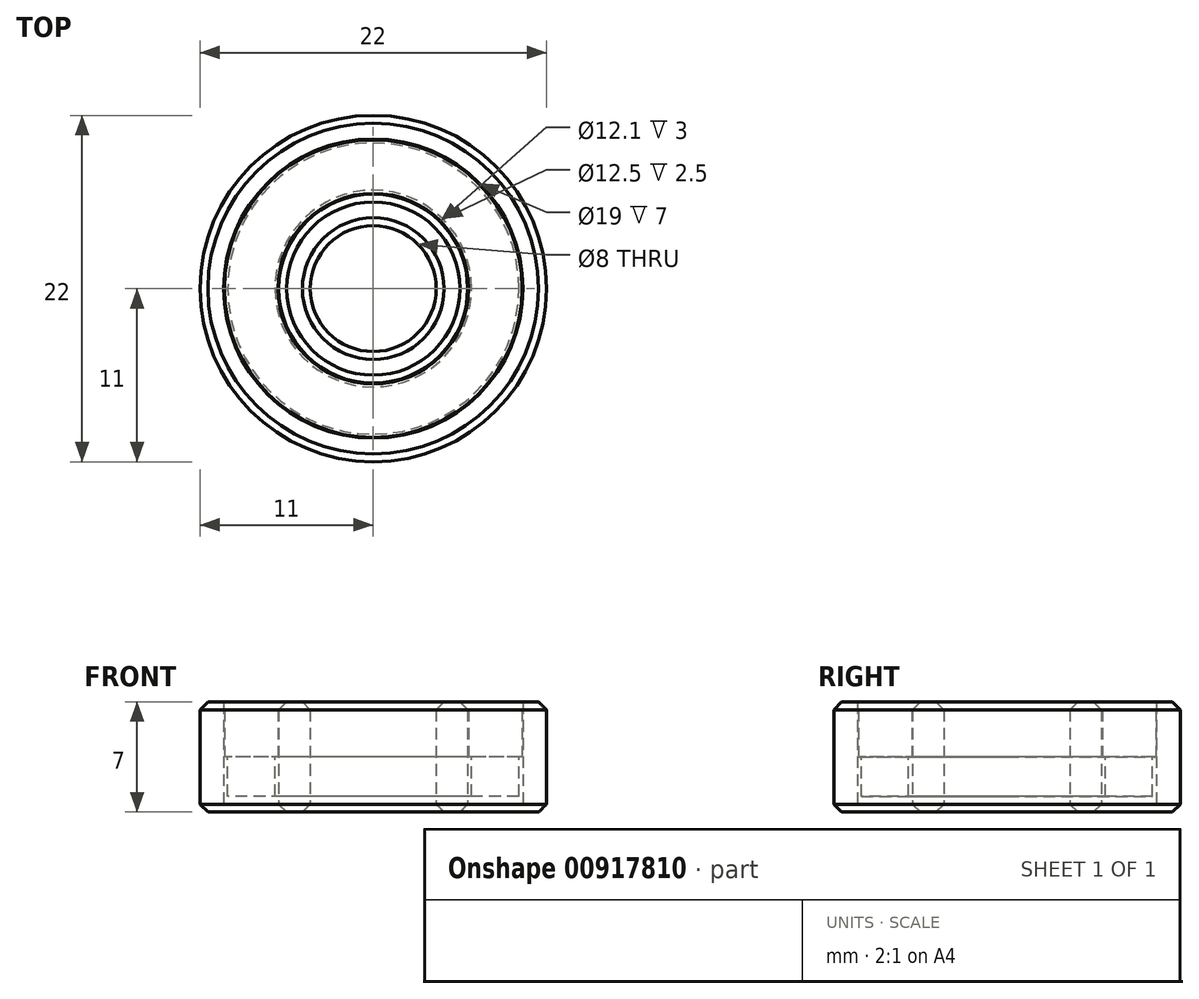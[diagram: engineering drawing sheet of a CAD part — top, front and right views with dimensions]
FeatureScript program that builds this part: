
annotation { "Feature Type Name" : "Feature", "Feature Type Description" : "" }
export const myFeature = defineFeature(function(context is Context, id is Id, definition is map)
    precondition{}
    {
        {
            var Q0;
            Q0=qCreatedBy(makeId("Top.planeOp"),FACE);
            var sketch = newSketch(context, id + "F0", { "sketchPlane" : qUnion([Q0])});
            skCircle(sketch, "E0", {"center": v(0, 0) * mm, "radius": 4 * mm});
            skCircle(sketch, "E1", {"center": v(0, 0) * mm, "radius": 6 * mm});
            skCircle(sketch, "E2", {"center": v(0, 0) * mm, "radius": 11 * mm});
            skCircle(sketch, "E3", {"center": v(0, 0) * mm, "radius": 9.5 * mm});
            skSolve(sketch);
        }
        {
            var Q0;
            Q0=makeQuery(id+"F0.imprint","IMPRINT",FACE,{"disambiguationData":[TD([[makeQuery(id+"F0.imprint","IMPRINT",EDGE,{"derivedFrom":sQuery(id+"F0.wireOp",EDGE,"E2")}),1.0]])]});
            var Q1;
            Q1=makeQuery(id+"F0.imprint","IMPRINT",FACE,{"disambiguationData":[TD([[makeQuery(id+"F0.imprint","IMPRINT",EDGE,{"derivedFrom":sQuery(id+"F0.wireOp",EDGE,"E0")}),-1.0]])]});
            extrude(context, id + "F1", {"entities" : qUnion([Q0, Q1]), "endBound" : BoundingType.SYMMETRIC, "depth" : 7 * mm, "offsetDistance" : 25 * mm});
        }
        {
            var Q0;
            Q0=qCreatedBy(makeId("Top.planeOp"),FACE);
            var sketch = newSketch(context, id + "F2", { "sketchPlane" : qUnion([Q0])});
            skCircle(sketch, "E4", {"center": v(0, 0) * mm, "radius": 6.25 * mm});
            skCircle(sketch, "E5", {"center": v(0, 0) * mm, "radius": 9.25 * mm});
            skSolve(sketch);
        }
        {
            var Q0;
            Q0=makeQuery(id+"F2.imprint","IMPRINT",FACE,{"disambiguationData":[TD([[makeQuery(id+"F2.imprint","IMPRINT",EDGE,{"derivedFrom":sQuery(id+"F2.wireOp",EDGE,"E4")}),-1.0]])]});
            extrude(context, id + "F3", {"entities" : qUnion([Q0]), "oppositeDirection" : true, "depth" : 2.5 * mm, "offsetDistance" : 25 * mm});
        }
        {
            var Q0;
            Q0=qCreatedBy(makeId("Top.planeOp"),FACE);
            var sketch = newSketch(context, id + "F4", { "sketchPlane" : qUnion([Q0])});
            skCircle(sketch, "E6", {"center": v(0, 0) * mm, "radius": 6.05 * mm});
            skCircle(sketch, "E7", {"center": v(0, 0) * mm, "radius": 9.45 * mm});
            skSolve(sketch);
        }
        {
            var Q0;
            Q0 = qSketchRegion(id + "F4", true);
            extrude(context, id + "F5", {"entities" : qUnion([Q0]), "depth" : 3 * mm, "offsetDistance" : 25 * mm});
        }
        {
            var Q0;
            Q0=makeQuery(id+"F1.opExtrude","CAP_EDGE",EDGE,{"disambiguationData":[OSD([sQuery(id+"F0.wireOp",EDGE,"E2")])],"isStart":false});
            var Q1;
            Q1=makeQuery(id+"F1.opExtrude","CAP_EDGE",EDGE,{"disambiguationData":[OSD([sQuery(id+"F0.wireOp",EDGE,"E2")])],"isStart":true});
            var Q2;
            Q2=makeQuery(id+"F1.opExtrude","CAP_EDGE",EDGE,{"disambiguationData":[OSD([sQuery(id+"F0.wireOp",EDGE,"E1")])],"isStart":false});
            var Q3;
            Q3=makeQuery(id+"F1.opExtrude","CAP_EDGE",EDGE,{"disambiguationData":[OSD([sQuery(id+"F0.wireOp",EDGE,"E0")])],"isStart":false});
            var Q4;
            Q4=makeQuery(id+"F1.opExtrude","CAP_EDGE",EDGE,{"disambiguationData":[OSD([sQuery(id+"F0.wireOp",EDGE,"E1")])],"isStart":true});
            var Q5;
            Q5=makeQuery(id+"F1.opExtrude","CAP_EDGE",EDGE,{"disambiguationData":[OSD([sQuery(id+"F0.wireOp",EDGE,"E0")])],"isStart":true});
            chamfer(context, id + "F6", {"entities" : qUnion([Q0, Q1, Q2, Q3, Q4, Q5]), "width" : 0.5 * mm, "tangentPropagation" : true});
        }
    });
